# Revit family: Series_500_XXXX_Standard
name_source: partatom
category: Windows
revit_build: Autodesk Revit 2014 (Build: 20130308_1515(x64)
units: mm (PartAtom-declared; Revit-internal decimal feet)

## types (78) — shared parameters
Astragal Sash Gap = 1 mm  [stored 0.00328084 ft]
Centered In Wall = Yes
Custom Sash Width Side = 800 mm  [stored 2.62467 ft]
Default Sill Height = 800 mm  [stored 2.62467 ft]
Description = 500 Slenderline Sliding Window
Equal Sash Width = Yes
Frame Thickness = 54 mm
Glass Type = Glass
Glazing Thickness = 4 mm  [stored 0.0131234 ft]
Heavy Duty Handle = No
Heavy Duty Handle Gap = 27 mm
Heavy Duty Interlocker = No
Limit Sash Height Max = 1500 mm  [stored 4.92126 ft]
Limit Sash Height Min = 300 mm  [stored 0.984252 ft]
Limit Sash Width Max = 750 mm  [stored 2.46063 ft]
Limit Sash Width Min = 300 mm  [stored 0.984252 ft]
Limit Window Height Max = 1575 mm
Limit Window Height Min = 375 mm
Limit Window Width Max = 3024 mm
Limit Window Width Min = 1224 mm
Model = 500 Slenderline Sliding Window
Sash Frame Seal = 1 mm  [stored 0.00328084 ft]
Sash Rail Fore Aft Spacing = 2 mm  [stored 0.00656168 ft]
Standard Interlocker = Yes
Wall Closure = By host
zero-valued in all types: Custom Frame Offset From Exterior, Is Heavy Duty Handle, Is Heavy Duty Mullion

## per-type parameters (varying)
| type | Area Middle Sash Glazing | Area Side Sash Glazing | Custom Windload | Custom Window Height | Custom Window Width | Height | Limit Sash Width Side Max | Limit Sash Width Side Min | Manufacturer | Max Pane Area | Sash Height | Sash Width Middle | Sash Width Sides | Width | Windload Design |
| 500SW-1206XXXX-1000Pa | 0.12 m² | 0.12 m² | 1000 mm  [stored 3.28084 ft] | 590 mm  [stored 1.9357 ft] | 1190 mm  [stored 3.9042 ft] | 590 mm  [stored 1.9357 ft] | 300 mm  [stored 0.984252 ft] | 300 mm  [stored 0.984252 ft] | Crealco | 0.12 m² | 515 mm | 300 mm  [stored 0.984252 ft] | 300 mm  [stored 0.984252 ft] | 1224 mm | 1000 mm  [stored 3.28084 ft] |
| 500SW-1206XXXX-1500Pa | 0.12 m² | 0.12 m² | 1500 mm  [stored 4.92126 ft] | 590 mm  [stored 1.9357 ft] | 1190 mm  [stored 3.9042 ft] | 590 mm  [stored 1.9357 ft] | 300 mm  [stored 0.984252 ft] | 300 mm  [stored 0.984252 ft] | Crealco | 0.12 m² | 515 mm | 300 mm  [stored 0.984252 ft] | 300 mm  [stored 0.984252 ft] | 1224 mm | 1500 mm  [stored 4.92126 ft] |
| 500SW-1206XXXX-2000Pa | 0.12 m² | 0.12 m² | 2000 mm  [stored 6.56168 ft] | 590 mm  [stored 1.9357 ft] | 1190 mm  [stored 3.9042 ft] | 590 mm  [stored 1.9357 ft] | 300 mm  [stored 0.984252 ft] | 300 mm  [stored 0.984252 ft] | Crealco | 0.12 m² | 515 mm | 300 mm  [stored 0.984252 ft] | 300 mm  [stored 0.984252 ft] | 1224 mm | 2000 mm  [stored 6.56168 ft] |
| 500SW-1506XXXX-1000Pa | 0.15 m² | 0.15 m² | 1000 mm  [stored 3.28084 ft] | 590 mm  [stored 1.9357 ft] | 1490 mm  [stored 4.88845 ft] | 590 mm  [stored 1.9357 ft] | 433 mm | 300 mm  [stored 0.984252 ft] | Crealco | 0.15 m² | 515 mm | 367 mm | 367 mm | 1490 mm  [stored 4.88845 ft] | 1000 mm  [stored 3.28084 ft] |
| 500SW-1506XXXX-1500Pa | 0.15 m² | 0.15 m² | 1500 mm  [stored 4.92126 ft] | 590 mm  [stored 1.9357 ft] | 1490 mm  [stored 4.88845 ft] | 590 mm  [stored 1.9357 ft] | 433 mm | 300 mm  [stored 0.984252 ft] | Crealco | 0.15 m² | 515 mm | 367 mm | 367 mm | 1490 mm  [stored 4.88845 ft] | 1500 mm  [stored 4.92126 ft] |
| 500SW-1506XXXX-2000Pa | 0.15 m² | 0.15 m² | 2000 mm  [stored 6.56168 ft] | 590 mm  [stored 1.9357 ft] | 1490 mm  [stored 4.88845 ft] | 590 mm  [stored 1.9357 ft] | 433 mm | 300 mm  [stored 0.984252 ft] | Crealco | 0.15 m² | 515 mm | 367 mm | 367 mm | 1490 mm  [stored 4.88845 ft] | 2000 mm  [stored 6.56168 ft] |
| 500SW-1806XXXX-1000Pa | 0.18 m² | 0.18 m² | 1000 mm  [stored 3.28084 ft] | 590 mm  [stored 1.9357 ft] | 1790 mm  [stored 5.8727 ft] | 590 mm  [stored 1.9357 ft] | 583 mm | 300 mm  [stored 0.984252 ft] | Crealco | 0.18 m² | 515 mm | 442 mm | 442 mm | 1790 mm  [stored 5.8727 ft] | 1000 mm  [stored 3.28084 ft] |
| 500SW-1806XXXX-1500Pa | 0.18 m² | 0.18 m² | 1500 mm  [stored 4.92126 ft] | 590 mm  [stored 1.9357 ft] | 1790 mm  [stored 5.8727 ft] | 590 mm  [stored 1.9357 ft] | 583 mm | 300 mm  [stored 0.984252 ft] | Crealco | 0.18 m² | 515 mm | 442 mm | 442 mm | 1790 mm  [stored 5.8727 ft] | 1500 mm  [stored 4.92126 ft] |
| 500SW-1806XXXX-2000Pa | 0.18 m² | 0.18 m² | 2000 mm  [stored 6.56168 ft] | 590 mm  [stored 1.9357 ft] | 1790 mm  [stored 5.8727 ft] | 590 mm  [stored 1.9357 ft] | 583 mm | 300 mm  [stored 0.984252 ft] | Crealco | 0.18 m² | 515 mm | 442 mm | 442 mm | 1790 mm  [stored 5.8727 ft] | 2000 mm  [stored 6.56168 ft] |
| 500SW-2106XXXX-1000Pa | 0.22 m² | 0.22 m² | 1000 mm  [stored 3.28084 ft] | 590 mm  [stored 1.9357 ft] | 2090 mm  [stored 6.85696 ft] | 590 mm  [stored 1.9357 ft] | 733 mm | 300 mm  [stored 0.984252 ft] | Crealco | 0.22 m² | 515 mm | 517 mm | 517 mm | 2090 mm  [stored 6.85696 ft] | 1000 mm  [stored 3.28084 ft] |
| 500SW-2106XXXX-1500Pa | 0.22 m² | 0.22 m² | 1500 mm  [stored 4.92126 ft] | 590 mm  [stored 1.9357 ft] | 2090 mm  [stored 6.85696 ft] | 590 mm  [stored 1.9357 ft] | 733 mm | 300 mm  [stored 0.984252 ft] | Crealco | 0.22 m² | 515 mm | 517 mm | 517 mm | 2090 mm  [stored 6.85696 ft] | 1500 mm  [stored 4.92126 ft] |
| 500SW-2106XXXX-2000Pa | 0.22 m² | 0.22 m² | 2000 mm  [stored 6.56168 ft] | 590 mm  [stored 1.9357 ft] | 2090 mm  [stored 6.85696 ft] | 590 mm  [stored 1.9357 ft] | 733 mm | 300 mm  [stored 0.984252 ft] | Crealco | 0.22 m² | 515 mm | 517 mm | 517 mm | 2090 mm  [stored 6.85696 ft] | 2000 mm  [stored 6.56168 ft] |
| 500SW-2406XXXX-1000Pa | 0.25 m² | 0.25 m² | 1000 mm  [stored 3.28084 ft] | 590 mm  [stored 1.9357 ft] | 2390 mm  [stored 7.84121 ft] | 590 mm  [stored 1.9357 ft] | 750 mm  [stored 2.46063 ft] | 433 mm | Crealco | 0.25 m² | 515 mm | 592 mm | 592 mm | 2390 mm  [stored 7.84121 ft] | 1000 mm  [stored 3.28084 ft] |
| 500SW-2406XXXX-1500Pa | 0.25 m² | 0.25 m² | 1500 mm  [stored 4.92126 ft] | 590 mm  [stored 1.9357 ft] | 2390 mm  [stored 7.84121 ft] | 590 mm  [stored 1.9357 ft] | 750 mm  [stored 2.46063 ft] | 433 mm | Crealco | 0.25 m² | 515 mm | 592 mm | 592 mm | 2390 mm  [stored 7.84121 ft] | 1500 mm  [stored 4.92126 ft] |
| 500SW-2406XXXX-2000Pa | 0.25 m² | 0.25 m² | 2000 mm  [stored 6.56168 ft] | 590 mm  [stored 1.9357 ft] | 2390 mm  [stored 7.84121 ft] | 590 mm  [stored 1.9357 ft] | 750 mm  [stored 2.46063 ft] | 433 mm | Crealco | 0.25 m² | 515 mm | 592 mm | 592 mm | 2390 mm  [stored 7.84121 ft] | 2000 mm  [stored 6.56168 ft] |
| 500SW-2706XXXX-1000Pa | 0.28 m² | 0.28 m² | 1000 mm  [stored 3.28084 ft] | 590 mm  [stored 1.9357 ft] | 2690 mm | 590 mm  [stored 1.9357 ft] | 750 mm  [stored 2.46063 ft] | 583 mm | Crealco | 0.28 m² | 515 mm | 667 mm | 667 mm | 2690 mm | 1000 mm  [stored 3.28084 ft] |
| 500SW-2706XXXX-1500Pa | 0.28 m² | 0.28 m² | 1500 mm  [stored 4.92126 ft] | 590 mm  [stored 1.9357 ft] | 2690 mm | 590 mm  [stored 1.9357 ft] | 750 mm  [stored 2.46063 ft] | 583 mm | Crealco | 0.28 m² | 515 mm | 667 mm | 667 mm | 2690 mm | 1500 mm  [stored 4.92126 ft] |
| 500SW-2706XXXX-2000Pa | 0.28 m² | 0.28 m² | 2000 mm  [stored 6.56168 ft] | 590 mm  [stored 1.9357 ft] | 2690 mm | 590 mm  [stored 1.9357 ft] | 750 mm  [stored 2.46063 ft] | 583 mm | Crealco | 0.28 m² | 515 mm | 667 mm | 667 mm | 2690 mm | 2000 mm  [stored 6.56168 ft] |
| 500SW-3006XXXX-1000Pa | 0.32 m² | 0.32 m² | 1000 mm  [stored 3.28084 ft] | 590 mm  [stored 1.9357 ft] | 2990 mm  [stored 9.80971 ft] | 590 mm  [stored 1.9357 ft] | 750 mm  [stored 2.46063 ft] | 733 mm | Crealco | 0.32 m² | 515 mm | 742 mm | 742 mm | 2990 mm  [stored 9.80971 ft] | 1000 mm  [stored 3.28084 ft] |
| 500SW-3006XXXX-1500Pa | 0.32 m² | 0.32 m² | 1500 mm  [stored 4.92126 ft] | 590 mm  [stored 1.9357 ft] | 2990 mm  [stored 9.80971 ft] | 590 mm  [stored 1.9357 ft] | 750 mm  [stored 2.46063 ft] | 733 mm | Crealco | 0.32 m² | 515 mm | 742 mm | 742 mm | 2990 mm  [stored 9.80971 ft] | 1500 mm  [stored 4.92126 ft] |
| 500SW-3006XXXX-2000Pa | 0.32 m² | 0.32 m² | 2000 mm  [stored 6.56168 ft] | 590 mm  [stored 1.9357 ft] | 2990 mm  [stored 9.80971 ft] | 590 mm  [stored 1.9357 ft] | 750 mm  [stored 2.46063 ft] | 733 mm | Crealco | 0.32 m² | 515 mm | 742 mm | 742 mm | 2990 mm  [stored 9.80971 ft] | 2000 mm  [stored 6.56168 ft] |
| 500SW-1209XXXX-1000Pa | 0.2 m² | 0.2 m² | 1000 mm  [stored 3.28084 ft] | 890 mm  [stored 2.91995 ft] | 1190 mm  [stored 3.9042 ft] | 890 mm  [stored 2.91995 ft] | 300 mm  [stored 0.984252 ft] | 300 mm  [stored 0.984252 ft] | Crealco | 0.2 m² | 815 mm | 300 mm  [stored 0.984252 ft] | 300 mm  [stored 0.984252 ft] | 1224 mm | 1000 mm  [stored 3.28084 ft] |
| 500SW-1209XXXX-1500Pa | 0.2 m² | 0.2 m² | 1500 mm  [stored 4.92126 ft] | 890 mm  [stored 2.91995 ft] | 1190 mm  [stored 3.9042 ft] | 890 mm  [stored 2.91995 ft] | 300 mm  [stored 0.984252 ft] | 300 mm  [stored 0.984252 ft] | Crealco | 0.2 m² | 815 mm | 300 mm  [stored 0.984252 ft] | 300 mm  [stored 0.984252 ft] | 1224 mm | 1500 mm  [stored 4.92126 ft] |
| 500SW-1209XXXX-2000Pa | 0.2 m² | 0.2 m² | 2000 mm  [stored 6.56168 ft] | 890 mm  [stored 2.91995 ft] | 1190 mm  [stored 3.9042 ft] | 890 mm  [stored 2.91995 ft] | 300 mm  [stored 0.984252 ft] | 300 mm  [stored 0.984252 ft] | Crealco | 0.2 m² | 815 mm | 300 mm  [stored 0.984252 ft] | 300 mm  [stored 0.984252 ft] | 1224 mm | 2000 mm  [stored 6.56168 ft] |
| 500SW-1509XXXX-1000Pa | 0.25 m² | 0.25 m² | 1000 mm  [stored 3.28084 ft] | 890 mm  [stored 2.91995 ft] | 1490 mm  [stored 4.88845 ft] | 890 mm  [stored 2.91995 ft] | 433 mm | 300 mm  [stored 0.984252 ft] | Crealco | 0.25 m² | 815 mm | 367 mm | 367 mm | 1490 mm  [stored 4.88845 ft] | 1000 mm  [stored 3.28084 ft] |
| 500SW-1509XXXX-1500Pa | 0.25 m² | 0.25 m² | 1500 mm  [stored 4.92126 ft] | 890 mm  [stored 2.91995 ft] | 1490 mm  [stored 4.88845 ft] | 890 mm  [stored 2.91995 ft] | 433 mm | 300 mm  [stored 0.984252 ft] | Crealco | 0.25 m² | 815 mm | 367 mm | 367 mm | 1490 mm  [stored 4.88845 ft] | 1500 mm  [stored 4.92126 ft] |
| 500SW-1509XXXX-2000Pa | 0.25 m² | 0.25 m² | 2000 mm  [stored 6.56168 ft] | 890 mm  [stored 2.91995 ft] | 1490 mm  [stored 4.88845 ft] | 890 mm  [stored 2.91995 ft] | 433 mm | 300 mm  [stored 0.984252 ft] | Crealco | 0.25 m² | 815 mm | 367 mm | 367 mm | 1490 mm  [stored 4.88845 ft] | 2000 mm  [stored 6.56168 ft] |
| 500SW-1809XXXX-1000Pa | 0.31 m² | 0.31 m² | 1000 mm  [stored 3.28084 ft] | 890 mm  [stored 2.91995 ft] | 1790 mm  [stored 5.8727 ft] | 890 mm  [stored 2.91995 ft] | 583 mm | 300 mm  [stored 0.984252 ft] | Crealco | 0.31 m² | 815 mm | 442 mm | 442 mm | 1790 mm  [stored 5.8727 ft] | 1000 mm  [stored 3.28084 ft] |
| 500SW-1809XXXX-1500Pa | 0.31 m² | 0.31 m² | 1500 mm  [stored 4.92126 ft] | 890 mm  [stored 2.91995 ft] | 1790 mm  [stored 5.8727 ft] | 890 mm  [stored 2.91995 ft] | 583 mm | 300 mm  [stored 0.984252 ft] | Crealco | 0.31 m² | 815 mm | 442 mm | 442 mm | 1790 mm  [stored 5.8727 ft] | 1500 mm  [stored 4.92126 ft] |
| 500SW-1809XXXX-2000Pa | 0.31 m² | 0.31 m² | 2000 mm  [stored 6.56168 ft] | 890 mm  [stored 2.91995 ft] | 1790 mm  [stored 5.8727 ft] | 890 mm  [stored 2.91995 ft] | 583 mm | 300 mm  [stored 0.984252 ft] | Crealco | 0.31 m² | 815 mm | 442 mm | 442 mm | 1790 mm  [stored 5.8727 ft] | 2000 mm  [stored 6.56168 ft] |
| 500SW-2109XXXX-1000Pa | 0.36 m² | 0.36 m² | 1000 mm  [stored 3.28084 ft] | 890 mm  [stored 2.91995 ft] | 2090 mm  [stored 6.85696 ft] | 890 mm  [stored 2.91995 ft] | 733 mm | 300 mm  [stored 0.984252 ft] | Crealco | 0.36 m² | 815 mm | 517 mm | 517 mm | 2090 mm  [stored 6.85696 ft] | 1000 mm  [stored 3.28084 ft] |
| 500SW-2109XXXX-1500Pa | 0.36 m² | 0.36 m² | 1500 mm  [stored 4.92126 ft] | 890 mm  [stored 2.91995 ft] | 2090 mm  [stored 6.85696 ft] | 890 mm  [stored 2.91995 ft] | 733 mm | 300 mm  [stored 0.984252 ft] | Crealco | 0.36 m² | 815 mm | 517 mm | 517 mm | 2090 mm  [stored 6.85696 ft] | 1500 mm  [stored 4.92126 ft] |
| 500SW-2109XXXX-2000Pa | 0.36 m² | 0.36 m² | 2000 mm  [stored 6.56168 ft] | 890 mm  [stored 2.91995 ft] | 2090 mm  [stored 6.85696 ft] | 890 mm  [stored 2.91995 ft] | 733 mm | 300 mm  [stored 0.984252 ft] | Crealco | 0.36 m² | 815 mm | 517 mm | 517 mm | 2090 mm  [stored 6.85696 ft] | 2000 mm  [stored 6.56168 ft] |
| 500SW-2409XXXX-1000Pa | 0.42 m² | 0.42 m² | 1000 mm  [stored 3.28084 ft] | 890 mm  [stored 2.91995 ft] | 2390 mm  [stored 7.84121 ft] | 890 mm  [stored 2.91995 ft] | 750 mm  [stored 2.46063 ft] | 433 mm | Crealco | 0.42 m² | 815 mm | 592 mm | 592 mm | 2390 mm  [stored 7.84121 ft] | 1000 mm  [stored 3.28084 ft] |
| 500SW-2409XXXX-1500Pa | 0.42 m² | 0.42 m² | 1500 mm  [stored 4.92126 ft] | 890 mm  [stored 2.91995 ft] | 2390 mm  [stored 7.84121 ft] | 890 mm  [stored 2.91995 ft] | 750 mm  [stored 2.46063 ft] | 433 mm | Crealco | 0.42 m² | 815 mm | 592 mm | 592 mm | 2390 mm  [stored 7.84121 ft] | 1500 mm  [stored 4.92126 ft] |
| 500SW-2409XXXX-2000Pa | 0.42 m² | 0.42 m² | 2000 mm  [stored 6.56168 ft] | 890 mm  [stored 2.91995 ft] | 2390 mm  [stored 7.84121 ft] | 890 mm  [stored 2.91995 ft] | 750 mm  [stored 2.46063 ft] | 433 mm | Crealco | 0.42 m² | 815 mm | 592 mm | 592 mm | 2390 mm  [stored 7.84121 ft] | 2000 mm  [stored 6.56168 ft] |
| 500SW-2709XXXX-1000Pa | 0.47 m² | 0.47 m² | 1000 mm  [stored 3.28084 ft] | 890 mm  [stored 2.91995 ft] | 2690 mm | 890 mm  [stored 2.91995 ft] | 750 mm  [stored 2.46063 ft] | 583 mm | Crealco | 0.47 m² | 815 mm | 667 mm | 667 mm | 2690 mm | 1000 mm  [stored 3.28084 ft] |
| 500SW-2709XXXX-1500Pa | 0.47 m² | 0.47 m² | 1500 mm  [stored 4.92126 ft] | 890 mm  [stored 2.91995 ft] | 2690 mm | 890 mm  [stored 2.91995 ft] | 750 mm  [stored 2.46063 ft] | 583 mm | Crealco | 0.47 m² | 815 mm | 667 mm | 667 mm | 2690 mm | 1500 mm  [stored 4.92126 ft] |
| 500SW-2709XXXX-2000Pa | 0.47 m² | 0.47 m² | 2000 mm  [stored 6.56168 ft] | 890 mm  [stored 2.91995 ft] | 2690 mm | 890 mm  [stored 2.91995 ft] | 750 mm  [stored 2.46063 ft] | 583 mm | Crealco | 0.47 m² | 815 mm | 667 mm | 667 mm | 2690 mm | 2000 mm  [stored 6.56168 ft] |
| 500SW-3009XXXX-1000Pa | 0.53 m² | 0.53 m² | 1000 mm  [stored 3.28084 ft] | 890 mm  [stored 2.91995 ft] | 2990 mm  [stored 9.80971 ft] | 890 mm  [stored 2.91995 ft] | 750 mm  [stored 2.46063 ft] | 733 mm | Crealco | 0.53 m² | 815 mm | 742 mm | 742 mm | 2990 mm  [stored 9.80971 ft] | 1000 mm  [stored 3.28084 ft] |
| 500SW-3009XXXX-1500Pa | 0.53 m² | 0.53 m² | 1500 mm  [stored 4.92126 ft] | 890 mm  [stored 2.91995 ft] | 2990 mm  [stored 9.80971 ft] | 890 mm  [stored 2.91995 ft] | 750 mm  [stored 2.46063 ft] | 733 mm | Crealco | 0.53 m² | 815 mm | 742 mm | 742 mm | 2990 mm  [stored 9.80971 ft] | 1500 mm  [stored 4.92126 ft] |
| 500SW-3009XXXX-2000Pa | 0.53 m² | 0.53 m² | 2000 mm  [stored 6.56168 ft] | 890 mm  [stored 2.91995 ft] | 2990 mm  [stored 9.80971 ft] | 890 mm  [stored 2.91995 ft] | 750 mm  [stored 2.46063 ft] | 733 mm | Crealco | 0.53 m² | 815 mm | 742 mm | 742 mm | 2990 mm  [stored 9.80971 ft] | 2000 mm  [stored 6.56168 ft] |
| 500SW-1212XXXX-1000Pa | 0.28 m² | 0.28 m² | 1000 mm  [stored 3.28084 ft] | 1190 mm  [stored 3.9042 ft] | 1190 mm  [stored 3.9042 ft] | 1190 mm  [stored 3.9042 ft] | 300 mm  [stored 0.984252 ft] | 300 mm  [stored 0.984252 ft] | Crealco | 0.28 m² | 1115 mm | 300 mm  [stored 0.984252 ft] | 300 mm  [stored 0.984252 ft] | 1224 mm | 1000 mm  [stored 3.28084 ft] |
| 500SW-1212XXXX-1500Pa | 0.28 m² | 0.28 m² | 1500 mm  [stored 4.92126 ft] | 1190 mm  [stored 3.9042 ft] | 1190 mm  [stored 3.9042 ft] | 1190 mm  [stored 3.9042 ft] | 300 mm  [stored 0.984252 ft] | 300 mm  [stored 0.984252 ft] | Crealco | 0.28 m² | 1115 mm | 300 mm  [stored 0.984252 ft] | 300 mm  [stored 0.984252 ft] | 1224 mm | 1500 mm  [stored 4.92126 ft] |
| 500SW-1212XXXX-2000Pa | 0.28 m² | 0.28 m² | 2000 mm  [stored 6.56168 ft] | 1190 mm  [stored 3.9042 ft] | 1190 mm  [stored 3.9042 ft] | 1190 mm  [stored 3.9042 ft] | 300 mm  [stored 0.984252 ft] | 300 mm  [stored 0.984252 ft] |  | 0.28 m² | 1115 mm | 300 mm  [stored 0.984252 ft] | 300 mm  [stored 0.984252 ft] | 1224 mm | 2000 mm  [stored 6.56168 ft] |
| 500SW-1512XXXX-1000Pa | 0.35 m² | 0.35 m² | 1000 mm  [stored 3.28084 ft] | 1190 mm  [stored 3.9042 ft] | 1490 mm  [stored 4.88845 ft] | 1190 mm  [stored 3.9042 ft] | 433 mm | 300 mm  [stored 0.984252 ft] | Crealco | 0.35 m² | 1115 mm | 367 mm | 367 mm | 1490 mm  [stored 4.88845 ft] | 1000 mm  [stored 3.28084 ft] |
| 500SW-1512XXXX-1500Pa | 0.35 m² | 0.35 m² | 1500 mm  [stored 4.92126 ft] | 1190 mm  [stored 3.9042 ft] | 1490 mm  [stored 4.88845 ft] | 1190 mm  [stored 3.9042 ft] | 433 mm | 300 mm  [stored 0.984252 ft] | Crealco | 0.35 m² | 1115 mm | 367 mm | 367 mm | 1490 mm  [stored 4.88845 ft] | 1500 mm  [stored 4.92126 ft] |
| 500SW-1512XXXX-2000Pa | 0.35 m² | 0.35 m² | 2000 mm  [stored 6.56168 ft] | 1190 mm  [stored 3.9042 ft] | 1490 mm  [stored 4.88845 ft] | 1190 mm  [stored 3.9042 ft] | 433 mm | 300 mm  [stored 0.984252 ft] | Crealco | 0.35 m² | 1115 mm | 367 mm | 367 mm | 1490 mm  [stored 4.88845 ft] | 2000 mm  [stored 6.56168 ft] |
| 500SW-1812XXXX-1000Pa | 0.43 m² | 0.43 m² | 1000 mm  [stored 3.28084 ft] | 1190 mm  [stored 3.9042 ft] | 1790 mm  [stored 5.8727 ft] | 1190 mm  [stored 3.9042 ft] | 583 mm | 300 mm  [stored 0.984252 ft] | Crealco | 0.43 m² | 1115 mm | 442 mm | 442 mm | 1790 mm  [stored 5.8727 ft] | 1000 mm  [stored 3.28084 ft] |
| 500SW-1812XXXX-1500Pa | 0.43 m² | 0.43 m² | 1500 mm  [stored 4.92126 ft] | 1190 mm  [stored 3.9042 ft] | 1790 mm  [stored 5.8727 ft] | 1190 mm  [stored 3.9042 ft] | 583 mm | 300 mm  [stored 0.984252 ft] | Crealco | 0.43 m² | 1115 mm | 442 mm | 442 mm | 1790 mm  [stored 5.8727 ft] | 1500 mm  [stored 4.92126 ft] |
| 500SW-1812XXXX-2000Pa | 0.43 m² | 0.43 m² | 2000 mm  [stored 6.56168 ft] | 1190 mm  [stored 3.9042 ft] | 1790 mm  [stored 5.8727 ft] | 1190 mm  [stored 3.9042 ft] | 583 mm | 300 mm  [stored 0.984252 ft] | Crealco | 0.43 m² | 1115 mm | 442 mm | 442 mm | 1790 mm  [stored 5.8727 ft] | 2000 mm  [stored 6.56168 ft] |
| 500SW-2112XXXX-1000Pa | 0.51 m² | 0.51 m² | 1000 mm  [stored 3.28084 ft] | 1190 mm  [stored 3.9042 ft] | 2090 mm  [stored 6.85696 ft] | 1190 mm  [stored 3.9042 ft] | 733 mm | 300 mm  [stored 0.984252 ft] | Crealco | 0.51 m² | 1115 mm | 517 mm | 517 mm | 2090 mm  [stored 6.85696 ft] | 1000 mm  [stored 3.28084 ft] |
| 500SW-2112XXXX-1500Pa | 0.51 m² | 0.51 m² | 1500 mm  [stored 4.92126 ft] | 1190 mm  [stored 3.9042 ft] | 2090 mm  [stored 6.85696 ft] | 1190 mm  [stored 3.9042 ft] | 733 mm | 300 mm  [stored 0.984252 ft] | Crealco | 0.51 m² | 1115 mm | 517 mm | 517 mm | 2090 mm  [stored 6.85696 ft] | 1500 mm  [stored 4.92126 ft] |
| 500SW-2112XXXX-2000Pa | 0.51 m² | 0.51 m² | 2000 mm  [stored 6.56168 ft] | 1190 mm  [stored 3.9042 ft] | 2090 mm  [stored 6.85696 ft] | 1190 mm  [stored 3.9042 ft] | 733 mm | 300 mm  [stored 0.984252 ft] | Crealco | 0.51 m² | 1115 mm | 517 mm | 517 mm | 2090 mm  [stored 6.85696 ft] | 2000 mm  [stored 6.56168 ft] |
| 500SW-2412XXXX-1000Pa | 0.59 m² | 0.59 m² | 1000 mm  [stored 3.28084 ft] | 1190 mm  [stored 3.9042 ft] | 2390 mm  [stored 7.84121 ft] | 1190 mm  [stored 3.9042 ft] | 750 mm  [stored 2.46063 ft] | 433 mm | Crealco | 0.59 m² | 1115 mm | 592 mm | 592 mm | 2390 mm  [stored 7.84121 ft] | 1000 mm  [stored 3.28084 ft] |
| 500SW-2412XXXX-1500Pa | 0.59 m² | 0.59 m² | 1500 mm  [stored 4.92126 ft] | 1190 mm  [stored 3.9042 ft] | 2390 mm  [stored 7.84121 ft] | 1190 mm  [stored 3.9042 ft] | 750 mm  [stored 2.46063 ft] | 433 mm | Crealco | 0.59 m² | 1115 mm | 592 mm | 592 mm | 2390 mm  [stored 7.84121 ft] | 1500 mm  [stored 4.92126 ft] |
| 500SW-2412XXXX-2000Pa | 0.59 m² | 0.59 m² | 2000 mm  [stored 6.56168 ft] | 1190 mm  [stored 3.9042 ft] | 2390 mm  [stored 7.84121 ft] | 1190 mm  [stored 3.9042 ft] | 750 mm  [stored 2.46063 ft] | 433 mm | Crealco | 0.59 m² | 1115 mm | 592 mm | 592 mm | 2390 mm  [stored 7.84121 ft] | 2000 mm  [stored 6.56168 ft] |
| 500SW-2712XXXX-1000Pa | 0.66 m² | 0.66 m² | 1000 mm  [stored 3.28084 ft] | 1190 mm  [stored 3.9042 ft] | 2690 mm | 1190 mm  [stored 3.9042 ft] | 750 mm  [stored 2.46063 ft] | 583 mm | Crealco | 0.66 m² | 1115 mm | 667 mm | 667 mm | 2690 mm | 1000 mm  [stored 3.28084 ft] |
| 500SW-2712XXXX-1500Pa | 0.66 m² | 0.66 m² | 1500 mm  [stored 4.92126 ft] | 1190 mm  [stored 3.9042 ft] | 2690 mm | 1190 mm  [stored 3.9042 ft] | 750 mm  [stored 2.46063 ft] | 583 mm | Crealco | 0.66 m² | 1115 mm | 667 mm | 667 mm | 2690 mm | 1500 mm  [stored 4.92126 ft] |
| 500SW-2712XXXX-2000Pa | 0.66 m² | 0.66 m² | 2000 mm  [stored 6.56168 ft] | 1190 mm  [stored 3.9042 ft] | 2690 mm | 1190 mm  [stored 3.9042 ft] | 750 mm  [stored 2.46063 ft] | 583 mm | Crealco | 0.66 m² | 1115 mm | 667 mm | 667 mm | 2690 mm | 2000 mm  [stored 6.56168 ft] |
| 500SW-3012XXXX-1000Pa | 0.74 m² | 0.74 m² | 1000 mm  [stored 3.28084 ft] | 1190 mm  [stored 3.9042 ft] | 2990 mm  [stored 9.80971 ft] | 1190 mm  [stored 3.9042 ft] | 750 mm  [stored 2.46063 ft] | 733 mm | Crealco | 0.74 m² | 1115 mm | 742 mm | 742 mm | 2990 mm  [stored 9.80971 ft] | 1000 mm  [stored 3.28084 ft] |
| 500SW-3012XXXX-1500Pa | 0.74 m² | 0.74 m² | 1500 mm  [stored 4.92126 ft] | 1190 mm  [stored 3.9042 ft] | 2990 mm  [stored 9.80971 ft] | 1190 mm  [stored 3.9042 ft] | 750 mm  [stored 2.46063 ft] | 733 mm | Crealco | 0.74 m² | 1115 mm | 742 mm | 742 mm | 2990 mm  [stored 9.80971 ft] | 1500 mm  [stored 4.92126 ft] |
| 500SW-3012XXXX-2000Pa | 0.74 m² | 0.74 m² | 2000 mm  [stored 6.56168 ft] | 1190 mm  [stored 3.9042 ft] | 2990 mm  [stored 9.80971 ft] | 1190 mm  [stored 3.9042 ft] | 750 mm  [stored 2.46063 ft] | 733 mm | Crealco | 0.74 m² | 1115 mm | 742 mm | 742 mm | 2990 mm  [stored 9.80971 ft] | 2000 mm  [stored 6.56168 ft] |
| 500SW-1215XXXX-1000Pa | 0.36 m² | 0.36 m² | 1000 mm  [stored 3.28084 ft] | 1490 mm  [stored 4.88845 ft] | 1190 mm  [stored 3.9042 ft] | 1490 mm  [stored 4.88845 ft] | 300 mm  [stored 0.984252 ft] | 300 mm  [stored 0.984252 ft] | Crealco | 0.36 m² | 1415 mm  [stored 4.64239 ft] | 300 mm  [stored 0.984252 ft] | 300 mm  [stored 0.984252 ft] | 1224 mm | 1000 mm  [stored 3.28084 ft] |
| 500SW-1215XXXX-1500Pa | 0.36 m² | 0.36 m² | 1500 mm  [stored 4.92126 ft] | 1490 mm  [stored 4.88845 ft] | 1190 mm  [stored 3.9042 ft] | 1490 mm  [stored 4.88845 ft] | 300 mm  [stored 0.984252 ft] | 300 mm  [stored 0.984252 ft] | Crealco | 0.36 m² | 1415 mm  [stored 4.64239 ft] | 300 mm  [stored 0.984252 ft] | 300 mm  [stored 0.984252 ft] | 1224 mm | 1500 mm  [stored 4.92126 ft] |
| 500SW-1215XXXX-2000Pa | 0.36 m² | 0.36 m² | 2000 mm  [stored 6.56168 ft] | 1490 mm  [stored 4.88845 ft] | 1190 mm  [stored 3.9042 ft] | 1490 mm  [stored 4.88845 ft] | 300 mm  [stored 0.984252 ft] | 300 mm  [stored 0.984252 ft] | Crealco | 0.36 m² | 1415 mm  [stored 4.64239 ft] | 300 mm  [stored 0.984252 ft] | 300 mm  [stored 0.984252 ft] | 1224 mm | 2000 mm  [stored 6.56168 ft] |
| 500SW-1515XXXX-1000Pa | 0.45 m² | 0.45 m² | 1000 mm  [stored 3.28084 ft] | 1490 mm  [stored 4.88845 ft] | 1490 mm  [stored 4.88845 ft] | 1490 mm  [stored 4.88845 ft] | 433 mm | 300 mm  [stored 0.984252 ft] | Crealco | 0.45 m² | 1415 mm  [stored 4.64239 ft] | 367 mm | 367 mm | 1490 mm  [stored 4.88845 ft] | 1000 mm  [stored 3.28084 ft] |
| 500SW-1515XXXX-1500Pa | 0.45 m² | 0.45 m² | 1500 mm  [stored 4.92126 ft] | 1490 mm  [stored 4.88845 ft] | 1490 mm  [stored 4.88845 ft] | 1490 mm  [stored 4.88845 ft] | 433 mm | 300 mm  [stored 0.984252 ft] | Crealco | 0.45 m² | 1415 mm  [stored 4.64239 ft] | 367 mm | 367 mm | 1490 mm  [stored 4.88845 ft] | 1500 mm  [stored 4.92126 ft] |
| 500SW-1515XXXX-2000Pa | 0.45 m² | 0.45 m² | 2000 mm  [stored 6.56168 ft] | 1490 mm  [stored 4.88845 ft] | 1490 mm  [stored 4.88845 ft] | 1490 mm  [stored 4.88845 ft] | 433 mm | 300 mm  [stored 0.984252 ft] | Crealco | 0.45 m² | 1415 mm  [stored 4.64239 ft] | 367 mm | 367 mm | 1490 mm  [stored 4.88845 ft] | 2000 mm  [stored 6.56168 ft] |
| 500SW-1815XXXX-1000Pa | 0.55 m² | 0.55 m² | 1000 mm  [stored 3.28084 ft] | 1490 mm  [stored 4.88845 ft] | 1790 mm  [stored 5.8727 ft] | 1490 mm  [stored 4.88845 ft] | 583 mm | 300 mm  [stored 0.984252 ft] | Crealco | 0.55 m² | 1415 mm  [stored 4.64239 ft] | 442 mm | 442 mm | 1790 mm  [stored 5.8727 ft] | 1000 mm  [stored 3.28084 ft] |
| 500SW-1815XXXX-1500Pa | 0.55 m² | 0.55 m² | 1500 mm  [stored 4.92126 ft] | 1490 mm  [stored 4.88845 ft] | 1790 mm  [stored 5.8727 ft] | 1490 mm  [stored 4.88845 ft] | 583 mm | 300 mm  [stored 0.984252 ft] | Crealco | 0.55 m² | 1415 mm  [stored 4.64239 ft] | 442 mm | 442 mm | 1790 mm  [stored 5.8727 ft] | 1500 mm  [stored 4.92126 ft] |
| 500SW-1815XXXX-2000Pa | 0.55 m² | 0.55 m² | 2000 mm  [stored 6.56168 ft] | 1490 mm  [stored 4.88845 ft] | 1790 mm  [stored 5.8727 ft] | 1490 mm  [stored 4.88845 ft] | 583 mm | 300 mm  [stored 0.984252 ft] | Crealco | 0.55 m² | 1415 mm  [stored 4.64239 ft] | 442 mm | 442 mm | 1790 mm  [stored 5.8727 ft] | 2000 mm  [stored 6.56168 ft] |
| 500SW-2115XXXX-1000Pa | 0.65 m² | 0.65 m² | 1000 mm  [stored 3.28084 ft] | 1490 mm  [stored 4.88845 ft] | 2090 mm  [stored 6.85696 ft] | 1490 mm  [stored 4.88845 ft] | 733 mm | 300 mm  [stored 0.984252 ft] | Crealco | 0.65 m² | 1415 mm  [stored 4.64239 ft] | 517 mm | 517 mm | 2090 mm  [stored 6.85696 ft] | 1000 mm  [stored 3.28084 ft] |
| 500SW-2115XXXX-1500Pa | 0.65 m² | 0.65 m² | 1500 mm  [stored 4.92126 ft] | 1490 mm  [stored 4.88845 ft] | 2090 mm  [stored 6.85696 ft] | 1490 mm  [stored 4.88845 ft] | 733 mm | 300 mm  [stored 0.984252 ft] | Crealco | 0.65 m² | 1415 mm  [stored 4.64239 ft] | 517 mm | 517 mm | 2090 mm  [stored 6.85696 ft] | 1500 mm  [stored 4.92126 ft] |
| 500SW-2415XXXX-1000Pa | 0.75 m² | 0.75 m² | 1000 mm  [stored 3.28084 ft] | 1490 mm  [stored 4.88845 ft] | 2390 mm  [stored 7.84121 ft] | 1490 mm  [stored 4.88845 ft] | 750 mm  [stored 2.46063 ft] | 433 mm | Crealco | 0.75 m² | 1415 mm  [stored 4.64239 ft] | 592 mm | 592 mm | 2390 mm  [stored 7.84121 ft] | 1000 mm  [stored 3.28084 ft] |
| 500SW-2415XXXX-1500Pa | 0.75 m² | 0.75 m² | 1500 mm  [stored 4.92126 ft] | 1490 mm  [stored 4.88845 ft] | 2390 mm  [stored 7.84121 ft] | 1490 mm  [stored 4.88845 ft] | 750 mm  [stored 2.46063 ft] | 433 mm | Crealco | 0.75 m² | 1415 mm  [stored 4.64239 ft] | 592 mm | 592 mm | 2390 mm  [stored 7.84121 ft] | 1500 mm  [stored 4.92126 ft] |
| 500SW-2715XXXX-1000Pa | 0.85 m² | 0.85 m² | 1000 mm  [stored 3.28084 ft] | 1490 mm  [stored 4.88845 ft] | 2690 mm | 1490 mm  [stored 4.88845 ft] | 750 mm  [stored 2.46063 ft] | 583 mm | Crealco | 0.85 m² | 1415 mm  [stored 4.64239 ft] | 667 mm | 667 mm | 2690 mm | 1000 mm  [stored 3.28084 ft] |
| 500SW-3015XXXX-1000Pa | 0.96 m² | 0.96 m² | 1000 mm  [stored 3.28084 ft] | 1490 mm  [stored 4.88845 ft] | 2990 mm  [stored 9.80971 ft] | 1490 mm  [stored 4.88845 ft] | 750 mm  [stored 2.46063 ft] | 733 mm | Crealco | 0.96 m² | 1415 mm  [stored 4.64239 ft] | 742 mm | 742 mm | 2990 mm  [stored 9.80971 ft] | 1000 mm  [stored 3.28084 ft] |

note: [stored X ft] marks values corroborated as IEEE doubles in the binary element streams (Revit-internal decimal feet)

## geometry (parser evidence)
native form markers: Sweep x50
no freeform markers — native parametric forms only
